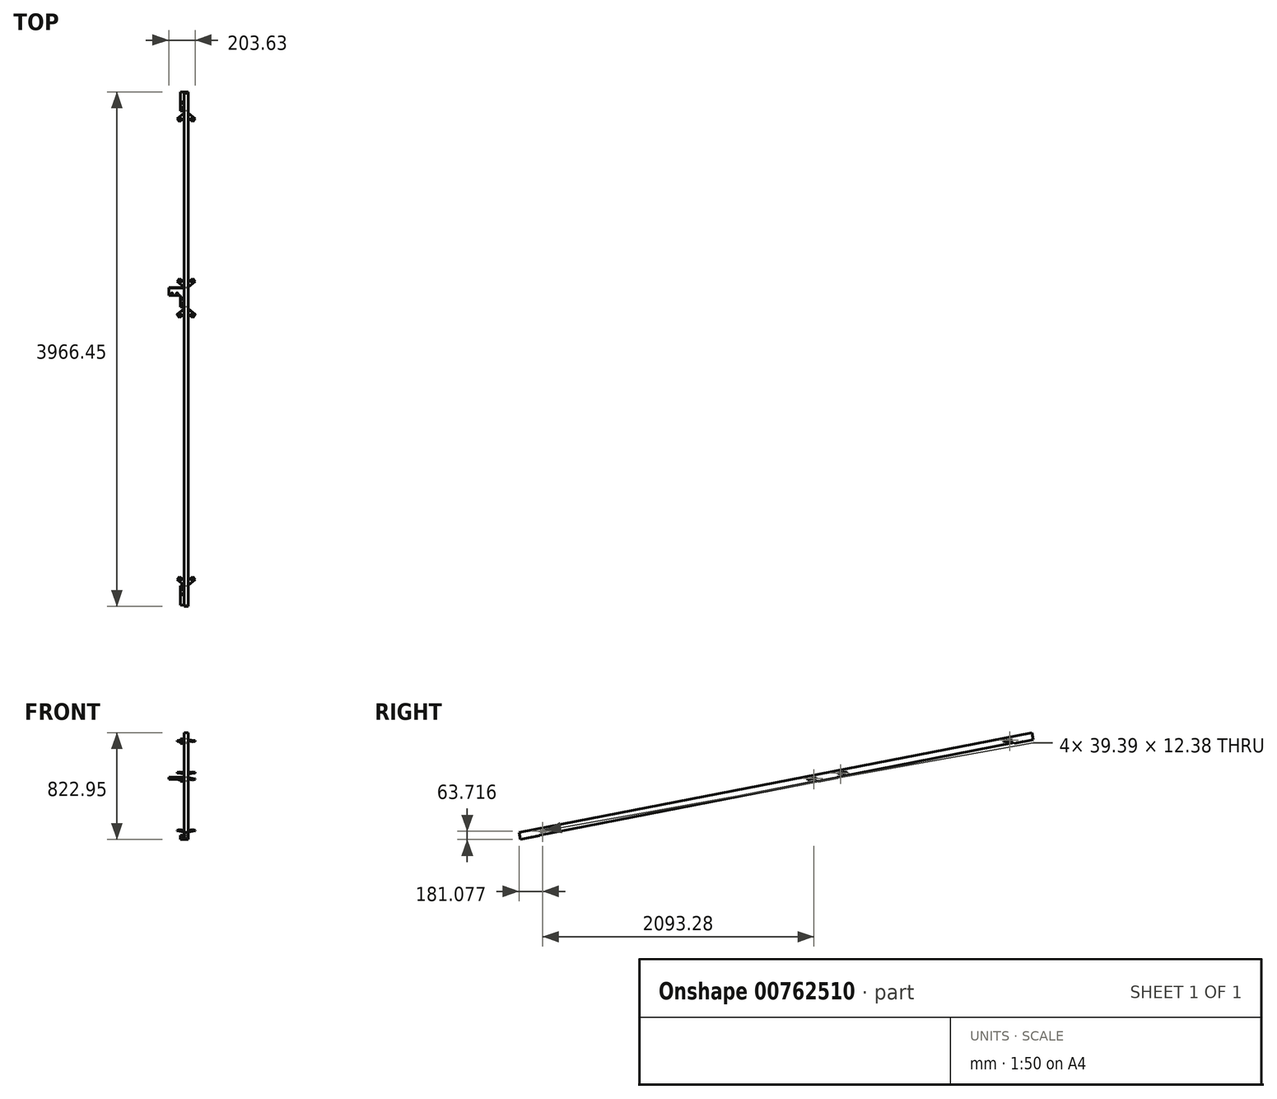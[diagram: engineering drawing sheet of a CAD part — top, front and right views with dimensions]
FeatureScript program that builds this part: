
annotation { "Feature Type Name" : "Feature", "Feature Type Description" : "" }
export const myFeature = defineFeature(function(context is Context, id is Id, definition is map)
    precondition{}
    {
        {
            var Q0;
            Q0=qCreatedBy(makeId("Top.planeOp"),FACE);
            var sketch = newSketch(context, id + "F0", { "sketchPlane" : qUnion([Q0])});
            skPoint(sketch, "E0", {"position": v(0, 0) * mm});
            skPoint(sketch, "E1", {"position": v(28.11, 0) * mm});
            skLineSegment(sketch, "E2", {"start": v(0, 0) * mm, "end": v(28.11, 0) * mm});
            skSolve(sketch);
        }
        {
            var Q0;
            Q0=qCreatedBy(makeId("Top.planeOp"),FACE);
            var Q1;
            Q1=sQuery(id+"F0.wireOp",EDGE,"E2");
            cPlane(context, id + "F1", {"entities" : qUnion([Q0, Q1]), "cplaneType" : CPlaneType.LINE_ANGLE, "offset" : 25 * mm, "angle" : 11 * degree, "width" : 150 * mm, "height" : 150 * mm});
        }
        {
            var Q0;
            Q0=qCreatedBy(id+"F1.planeOp",FACE);
            var Q1;
            Q1=sQuery(id+"F0.wireOp",EDGE,"E2");
            cPlane(context, id + "F2", {"entities" : qUnion([Q0, Q1]), "cplaneType" : CPlaneType.LINE_ANGLE, "offset" : 25 * mm, "angle" : 90 * degree, "width" : 150 * mm, "height" : 150 * mm});
        }
        {
            var Q0;
            Q0=qCreatedBy(id+"F2.planeOp",FACE);
            var sketch = newSketch(context, id + "F3", { "sketchPlane" : qUnion([Q0])});
            skLineSegment(sketch, "E3.bottom", {"start": v(15, -25) * mm, "end": v(-15, -25) * mm});
            skLineSegment(sketch, "E3.top", {"start": v(15, 25) * mm, "end": v(-15, 25) * mm});
            skLineSegment(sketch, "E3.left", {"start": v(15, -25) * mm, "end": v(15, 25) * mm});
            skLineSegment(sketch, "E3.right", {"start": v(-15, -25) * mm, "end": v(-15, 25) * mm});
            skPoint(sketch, "E3.middle", {"position": v(0, 0) * mm});
            skLineSegment(sketch, "E4.bottom", {"start": v(14, -24) * mm, "end": v(-14, -24) * mm});
            skLineSegment(sketch, "E4.top", {"start": v(14, 24) * mm, "end": v(-14, 24) * mm});
            skLineSegment(sketch, "E4.left", {"start": v(14, -24) * mm, "end": v(14, 24) * mm});
            skLineSegment(sketch, "E4.right", {"start": v(-14, -24) * mm, "end": v(-14, 24) * mm});
            skSolve(sketch);
        }
        {
            var Q0;
            Q0=qSketchRegion(id+"F3",true);
            extrude(context, id + "F4", {"entities" : qUnion([Q0]), "depth" : 30 * mm, "offsetDistance" : 25 * mm, "hasSecondDirection" : true, "secondDirectionOppositeDirection" : true, "secondDirectionDepth" : 4000 * mm});
        }
        {
            var Q0;
            Q0=makeQuery(id+"F4.opExtrude","SWEPT_FACE",FACE,{"disambiguationData":[OSD([sQuery(id+"F3.wireOp",EDGE,"E3.bottom")])]});
            var sketch = newSketch(context, id + "F5", { "sketchPlane" : qUnion([Q0])});
            skLineSegment(sketch, "E5.0", {"start": v(-15, -4000) * mm, "end": v(-15, -3850) * mm});
            skLineSegment(sketch, "E6", {"start": v(15, -4000) * mm, "end": v(-15, -4000) * mm, "construction": true});
            skLineSegment(sketch, "E7", {"start": v(0, -4000) * mm, "end": v(0, -3850) * mm, "construction": true});
            skLineSegment(sketch, "E8.MirrorCS", {"start": v(-45, -3940) * mm, "end": v(-45, -4000) * mm});
            skLineSegment(sketch, "E9.MirrorCS", {"start": v(-45, -3940) * mm, "end": v(-45, -3850) * mm});
            skCircle(sketch, "E10.MirrorC", {"center": v(-30, -3915) * mm, "radius": 6 * mm});
            skLineSegment(sketch, "E11.MirrorCS", {"start": v(15, -3850) * mm, "end": v(-45, -3850) * mm});
            skLineSegment(sketch, "E12.MirrorCS", {"start": v(-45, -3940) * mm, "end": v(-135, -3940) * mm});
            skLineSegment(sketch, "E13.MirrorCS", {"start": v(-135, -4000) * mm, "end": v(-135, -3940) * mm});
            skLineSegment(sketch, "E14.MirrorCS", {"start": v(-45, -4000) * mm, "end": v(-135, -4000) * mm});
            skCircle(sketch, "E15.MirrorC", {"center": v(-110, -3955) * mm, "radius": 6 * mm});
            skCircle(sketch, "E16.MirrorC", {"center": v(-70, -3955) * mm, "radius": 6 * mm});
            skLineSegment(sketch, "E17.MirrorCS", {"start": v(15, -4000) * mm, "end": v(-45, -4000) * mm});
            skCircle(sketch, "E18.MirrorC", {"center": v(-30, -3875) * mm, "radius": 6 * mm});
            skLineSegment(sketch, "E19", {"start": v(15, -4000) * mm, "end": v(15, -3850) * mm});
            skSolve(sketch);
        }
        {
            var Q0;
            {var subQ3=sQuery(id+"F5.wireOp",EDGE,"E5.0");Q0=makeQuery(id+"F5.imprint","IMPRINT",FACE,{"disambiguationData":[TD([[makeQuery(id+"F5.imprint","IMPRINT",EDGE,{"derivedFrom":subQ3}),-1.0]])]});}
            var Q1;
            {var subQ0=sQuery(id+"F5.wireOp",EDGE,"E5.0");Q1=makeQuery(id+"F5.imprint","IMPRINT",FACE,{"disambiguationData":[TD([[makeQuery(id+"F5.imprint","IMPRINT",EDGE,{"derivedFrom":subQ0}),1.0]])]});}
            extrude(context, id + "F6", {"entities" : qUnion([Q0, Q1]), "operationType" : NewBodyOperationType.ADD, "depth" : 5 * mm, "offsetDistance" : 25 * mm});
        }
        {
            var Q0;
            Q0=makeQuery(id+"F4.opExtrude","SWEPT_FACE",FACE,{"disambiguationData":[OSD([sQuery(id+"F3.wireOp",EDGE,"E3.bottom")])]});
            var sketch = newSketch(context, id + "F7", { "sketchPlane" : qUnion([Q0])});
            skLineSegment(sketch, "E20", {"start": v(-15, -2461.65) * mm, "end": v(-15, -2311.65) * mm});
            skLineSegment(sketch, "E21", {"start": v(15, -2311.65) * mm, "end": v(15, -2461.65) * mm});
            skLineSegment(sketch, "E22", {"start": v(15, -2461.65) * mm, "end": v(-15, -2461.65) * mm, "construction": true});
            skLineSegment(sketch, "E23", {"start": v(0, -2461.65) * mm, "end": v(0, -2311.65) * mm, "construction": true});
            skLineSegment(sketch, "E24.MirrorCS", {"start": v(15, -2461.65) * mm, "end": v(-135, -2461.65) * mm});
            skLineSegment(sketch, "E25.MirrorCS", {"start": v(-45, -2401.65) * mm, "end": v(-45, -2461.65) * mm});
            skCircle(sketch, "E26.MirrorC", {"center": v(-70, -2416.65) * mm, "radius": 6 * mm});
            skCircle(sketch, "E27.MirrorC", {"center": v(-110, -2416.65) * mm, "radius": 6 * mm});
            skCircle(sketch, "E28.MirrorC", {"center": v(-30, -2376.65) * mm, "radius": 6 * mm});
            skLineSegment(sketch, "E29.MirrorCS", {"start": v(-45, -2401.65) * mm, "end": v(-45, -2311.65) * mm});
            skCircle(sketch, "E30.MirrorC", {"center": v(-30, -2336.65) * mm, "radius": 6 * mm});
            skLineSegment(sketch, "E31.MirrorCS", {"start": v(15, -2311.65) * mm, "end": v(-45, -2311.65) * mm});
            skLineSegment(sketch, "E32.MirrorCS", {"start": v(-135, -2461.65) * mm, "end": v(-135, -2401.65) * mm});
            skLineSegment(sketch, "E33.MirrorCS", {"start": v(-45, -2401.65) * mm, "end": v(-135, -2401.65) * mm});
            skLineSegment(sketch, "E34.MirrorCS", {"start": v(15, -2401.65) * mm, "end": v(15, -2461.65) * mm});
            skLineSegment(sketch, "E35.MirrorCS", {"start": v(-45, -2461.65) * mm, "end": v(105, -2461.65) * mm});
            skLineSegment(sketch, "E36.MirrorCS", {"start": v(105, -2461.65) * mm, "end": v(105, -2401.65) * mm});
            skLineSegment(sketch, "E37.MirrorCS", {"start": v(15, -2401.65) * mm, "end": v(105, -2401.65) * mm});
            skCircle(sketch, "E38.MirrorC", {"center": v(40, -2416.65) * mm, "radius": 6 * mm});
            skCircle(sketch, "E39.MirrorC", {"center": v(80, -2416.65) * mm, "radius": 6 * mm});
            skSolve(sketch);
        }
        {
            var Q0;
            {var subQ0=sQuery(id+"F7.wireOp",EDGE,"E25.MirrorCS");Q0=makeQuery(id+"F7.imprint","IMPRINT",FACE,{"disambiguationData":[TD([[makeQuery(id+"F7.imprint","IMPRINT",EDGE,{"derivedFrom":subQ0}),-1.0]])]});}
            var Q1;
            {var subQ1=sQuery(id+"F7.wireOp",EDGE,"E20");Q1=makeQuery(id+"F7.imprint","IMPRINT",FACE,{"disambiguationData":[TD([[makeQuery(id+"F7.imprint","IMPRINT",EDGE,{"derivedFrom":subQ1}),-1.0]])]});}
            var Q2;
            {var subQ0=sQuery(id+"F7.wireOp",EDGE,"E20");Q2=makeQuery(id+"F7.imprint","IMPRINT",FACE,{"disambiguationData":[TD([[makeQuery(id+"F7.imprint","IMPRINT",EDGE,{"derivedFrom":subQ0}),1.0]])]});}
            var Q3;
            {var subQ0=sQuery(id+"F7.wireOp",EDGE,"E34.MirrorCS");Q3=makeQuery(id+"F7.imprint","IMPRINT",FACE,{"disambiguationData":[TD([[makeQuery(id+"F7.imprint","IMPRINT",EDGE,{"derivedFrom":subQ0}),1.0]])]});}
            extrude(context, id + "F8", {"entities" : qUnion([Q0, Q1, Q2, Q3]), "operationType" : NewBodyOperationType.ADD, "depth" : 5 * mm, "offsetDistance" : 25 * mm});
        }
        {
            var Q0;
            Q0=qCreatedBy(id+"F1.planeOp",FACE);
            var sketch = newSketch(context, id + "F9", { "sketchPlane" : qUnion([Q0])});
            skLineSegment(sketch, "E40.0", {"start": v(15, -3850) * mm, "end": v(45, -3850) * mm});
            skLineSegment(sketch, "E41", {"start": v(15, -3850) * mm, "end": v(15, -3840) * mm});
            skLineSegment(sketch, "E42", {"start": v(41, -1985.01) * mm, "end": v(15.07, -1985.01) * mm});
            skLineSegment(sketch, "E43.MirrorCS", {"start": v(15, -3840) * mm, "end": v(68.63, -3795) * mm});
            skLineSegment(sketch, "E44.MirrorCS", {"start": v(68.63, -3795) * mm, "end": v(49.34, -3772.03) * mm});
            skLineSegment(sketch, "E45.MirrorCS", {"start": v(49.34, -3772.03) * mm, "end": v(14.87, -3800.95) * mm});
            skCircle(sketch, "E46.MirrorC", {"center": v(43.27, -3796.7) * mm, "radius": 6 * mm});
            skLineSegment(sketch, "E47.MirrorCS", {"start": v(43.27, -3796.7) * mm, "end": v(58.99, -3783.52) * mm, "construction": true});
            skLineSegment(sketch, "E48", {"start": v(15, -3840) * mm, "end": v(14.87, -3800.95) * mm});
            skLineSegment(sketch, "E49.MirrorCS", {"start": v(15, -130.03) * mm, "end": v(68.63, -175.02) * mm});
            skCircle(sketch, "E50.MirrorC", {"center": v(43.27, -173.32) * mm, "radius": 6 * mm});
            skLineSegment(sketch, "E51.MirrorCS", {"start": v(43.27, -173.32) * mm, "end": v(58.99, -186.5) * mm, "construction": true});
            skLineSegment(sketch, "E52.MirrorCS", {"start": v(68.63, -175.02) * mm, "end": v(49.34, -198) * mm});
            skLineSegment(sketch, "E53.MirrorCS", {"start": v(49.34, -198) * mm, "end": v(14.87, -169.08) * mm});
            skLineSegment(sketch, "E54.MirrorCS", {"start": v(15, -130.03) * mm, "end": v(14.87, -169.08) * mm});
            skPoint(sketch, "E55.0", {"position": v(30, -2311.65) * mm});
            skLineSegment(sketch, "E56.0", {"start": v(15, -2311.65) * mm, "end": v(45, -2311.65) * mm});
            skLineSegment(sketch, "E57.0", {"start": v(15, -2461.65) * mm, "end": v(45, -2461.65) * mm});
            skLineSegment(sketch, "E58", {"start": v(15, -2311.65) * mm, "end": v(15, -2301.65) * mm});
            skLineSegment(sketch, "E59", {"start": v(15, -2461.65) * mm, "end": v(15, -2471.65) * mm});
            skLineSegment(sketch, "E60", {"start": v(15, -2301.65) * mm, "end": v(15, -130.03) * mm});
            skLineSegment(sketch, "E61", {"start": v(45.74, -1215.84) * mm, "end": v(15, -1215.84) * mm});
            skLineSegment(sketch, "E62.MirrorCS", {"start": v(49.34, -2233.67) * mm, "end": v(14.87, -2262.6) * mm});
            skLineSegment(sketch, "E63.MirrorCS", {"start": v(15, -2301.65) * mm, "end": v(14.87, -2262.6) * mm});
            skLineSegment(sketch, "E64.MirrorCS", {"start": v(15, -2301.65) * mm, "end": v(68.63, -2256.65) * mm});
            skLineSegment(sketch, "E65.MirrorCS", {"start": v(68.63, -2256.65) * mm, "end": v(49.34, -2233.67) * mm});
            skLineSegment(sketch, "E66.MirrorCS", {"start": v(43.27, -2258.35) * mm, "end": v(58.99, -2245.16) * mm, "construction": true});
            skCircle(sketch, "E67.MirrorC", {"center": v(43.27, -2258.35) * mm, "radius": 6 * mm});
            skLineSegment(sketch, "E68", {"start": v(15, -2471.65) * mm, "end": v(15, -3840) * mm});
            skLineSegment(sketch, "E69", {"start": v(29.54, -3155.82) * mm, "end": v(15, -3155.82) * mm});
            skLineSegment(sketch, "E70.MirrorCS", {"start": v(15, -2471.65) * mm, "end": v(68.63, -2516.64) * mm});
            skLineSegment(sketch, "E71.MirrorCS", {"start": v(15, -2471.65) * mm, "end": v(14.87, -2510.7) * mm});
            skLineSegment(sketch, "E72.MirrorCS", {"start": v(49.34, -2539.62) * mm, "end": v(14.87, -2510.7) * mm});
            skLineSegment(sketch, "E73.MirrorCS", {"start": v(68.63, -2516.64) * mm, "end": v(49.34, -2539.62) * mm});
            skCircle(sketch, "E74.MirrorC", {"center": v(43.27, -2514.94) * mm, "radius": 6 * mm});
            skLineSegment(sketch, "E75.MirrorCS", {"start": v(43.27, -2514.94) * mm, "end": v(58.99, -2528.13) * mm, "construction": true});
            skLineSegment(sketch, "E76", {"start": v(15, -3840) * mm, "end": v(-15, -3840.1) * mm, "construction": true});
            skLineSegment(sketch, "E77", {"start": v(0, -3840.05) * mm, "end": v(0, -129.98) * mm, "construction": true});
            skLineSegment(sketch, "E78", {"start": v(15, -130.03) * mm, "end": v(0, -129.98) * mm, "construction": true});
            skLineSegment(sketch, "E79.MirrorCS", {"start": v(-49.34, -198) * mm, "end": v(-14.87, -169.08) * mm});
            skLineSegment(sketch, "E80.MirrorCS", {"start": v(-68.63, -175.02) * mm, "end": v(-49.34, -198) * mm});
            skLineSegment(sketch, "E81.MirrorCS", {"start": v(-15, -130.03) * mm, "end": v(-68.63, -175.02) * mm});
            skCircle(sketch, "E82.MirrorC", {"center": v(-43.27, -173.32) * mm, "radius": 6 * mm});
            skLineSegment(sketch, "E83.MirrorCS", {"start": v(-43.27, -173.32) * mm, "end": v(-58.99, -186.5) * mm, "construction": true});
            skLineSegment(sketch, "E84.MirrorCS", {"start": v(-15, -2301.65) * mm, "end": v(-68.63, -2256.65) * mm});
            skCircle(sketch, "E85.MirrorC", {"center": v(-43.27, -2258.35) * mm, "radius": 6 * mm});
            skLineSegment(sketch, "E86.MirrorCS", {"start": v(-49.34, -2233.67) * mm, "end": v(-14.87, -2262.6) * mm});
            skLineSegment(sketch, "E87.MirrorCS", {"start": v(-15, -2301.65) * mm, "end": v(-15, -130.03) * mm});
            skLineSegment(sketch, "E88.MirrorCS", {"start": v(-68.63, -2256.65) * mm, "end": v(-49.34, -2233.67) * mm});
            skLineSegment(sketch, "E89.MirrorCS", {"start": v(-15, -2471.65) * mm, "end": v(-68.63, -2516.64) * mm});
            skLineSegment(sketch, "E90.MirrorCS", {"start": v(-49.34, -2539.62) * mm, "end": v(-14.87, -2510.7) * mm});
            skLineSegment(sketch, "E91.MirrorCS", {"start": v(-68.63, -2516.64) * mm, "end": v(-49.34, -2539.62) * mm});
            skCircle(sketch, "E92.MirrorC", {"center": v(-43.27, -2514.94) * mm, "radius": 6 * mm});
            skLineSegment(sketch, "E93.MirrorCS", {"start": v(-43.27, -2514.94) * mm, "end": v(-58.99, -2528.13) * mm, "construction": true});
            skLineSegment(sketch, "E94.MirrorCS", {"start": v(-15, -3840) * mm, "end": v(-68.63, -3795) * mm});
            skCircle(sketch, "E95.MirrorC", {"center": v(-43.27, -3796.7) * mm, "radius": 6 * mm});
            skLineSegment(sketch, "E96.MirrorCS", {"start": v(-49.34, -3772.03) * mm, "end": v(-14.87, -3800.95) * mm});
            skLineSegment(sketch, "E97.MirrorCS", {"start": v(-68.63, -3795) * mm, "end": v(-49.34, -3772.03) * mm});
            skLineSegment(sketch, "E98.MirrorCS", {"start": v(-43.27, -3796.7) * mm, "end": v(-58.99, -3783.52) * mm, "construction": true});
            skLineSegment(sketch, "E99", {"start": v(-15, -3840) * mm, "end": v(-14.87, -3800.95) * mm});
            skLineSegment(sketch, "E100", {"start": v(-14.87, -2510.7) * mm, "end": v(-15, -2471.65) * mm});
            skSolve(sketch);
        }
        {
            var Q0;
            Q0=qSketchRegion(id+"F9",true);
            extrude(context, id + "F10", {"entities" : qUnion([Q0]), "operationType" : NewBodyOperationType.ADD, "depth" : 2.5 * mm, "offsetDistance" : 25 * mm, "hasSecondDirection" : true, "secondDirectionOppositeDirection" : true, "secondDirectionDepth" : 2.5 * mm});
        }
        {
            var Q0;
            {var subQ2=sQuery(id+"F7.wireOp",EDGE,"E31.MirrorCS");var subQ3=sQuery(id+"F3.wireOp",EDGE,"E3.bottom");Q0=makeQuery(id+"F8.boolean.opBoolean","SPLIT",FACE,{"disambiguationData":[TD([makeQuery(id+"F8.opExtrude","SWEPT_FACE",FACE,{"disambiguationData":[OSD([subQ2])]})])],"derivedFrom":makeQuery(id+"F4.opExtrude","SWEPT_FACE",FACE,{"disambiguationData":[OSD([subQ3])]})});}
            var sketch = newSketch(context, id + "F11", { "sketchPlane" : qUnion([Q0])});
            skLineSegment(sketch, "E101", {"start": v(-15, -120) * mm, "end": v(15, -120) * mm});
            skLineSegment(sketch, "E102.MirrorCS", {"start": v(15, -120) * mm, "end": v(-45, -120) * mm});
            skLineSegment(sketch, "E103.MirrorCS", {"start": v(-45, -30) * mm, "end": v(-45, -120) * mm});
            skCircle(sketch, "E104.MirrorC", {"center": v(-30, -55) * mm, "radius": 6 * mm});
            skCircle(sketch, "E105.MirrorC", {"center": v(-30, -95) * mm, "radius": 6 * mm});
            skLineSegment(sketch, "E106", {"start": v(-45, -30) * mm, "end": v(-45, 30) * mm});
            skLineSegment(sketch, "E107", {"start": v(15, 30) * mm, "end": v(-45, 30) * mm});
            skLineSegment(sketch, "E108", {"start": v(15, -120) * mm, "end": v(15, 30) * mm});
            skSolve(sketch);
        }
        {
            var Q0;
            Q0 = qSketchRegion(id + "F11", true);
            extrude(context, id + "F12", {"entities" : qUnion([Q0]), "operationType" : NewBodyOperationType.ADD, "depth" : 5 * mm, "offsetDistance" : 25 * mm});
        }
    });
